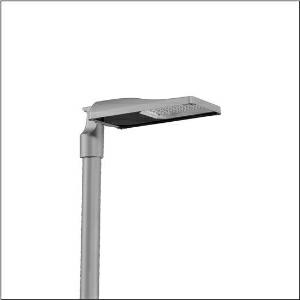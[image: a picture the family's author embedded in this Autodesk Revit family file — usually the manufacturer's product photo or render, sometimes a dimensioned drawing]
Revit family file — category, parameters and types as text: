
# Revit family: streetlight_sl_31_mini___st1_0a_5xh6d31b08ja_158d
name_source: partatom
category: Lighting Fixtures
units: mm (PartAtom-declared; Revit-internal decimal feet)

## family parameters
Cut with Voids When Loaded = No
Host = Face
Light Source = No
Part Type = Normal
Room Calculation Point = No
Round Connector Dimension = Use Diameter
Shared = No

## types (1)
- --- (1 x LED, 12140 lm, 81.1 W, 3000K)
    Apparent Load = 81 VA
    CIE Flux Codes = 40 73 97 100 100
    Color Rendering = 70
    Color Temperature = 3000K
    Default Elevation = 1800 mm
    Description = Streetlight SL 31 mini Easy, LST, Desk-Remote mast luminaire for post-top, side-entry; light control with lens of PMMA; light distribution: ST1.0a, direct asymmetric distribution, for standard-compliant lighting for roads and squares; LED: luminous flux: 12.140lm, light colour: 730, colour temperature: 3000K; luminous efficacy: 149,7lm/W; control: pre-setting: linear dimming characteristic, flexible luminous flux parameterisation, time-dependent luminous flux control, constant luminous flux control, power reduction, intelligent temperature release in ECG and LED module, overheat protection; luminaire housing, of diecast aluminium, SITECO metallic grey (DB 702S), corrosivity category C5 high according to DIN EN ISO 12944; cover of toughened safety glass, transparent, opened without tools; mast flange of diecast aluminium, SITECO metallic grey (DB 702S), spigot size: 76/60mm, mast flange included unmounted; with cable H07RN-F 5x 1.5mm², cable length: 10,5m, connection cable pre-assembled; mains connection: 220..240V, AC, 50/60Hz; power consumption (at start of service life): 81,1W / (at end of service life): 88,3W / (with reduced operation 50%): 36,4W; protection rating (complete): IP66; insulation class (complete): insulation class II (safety insulation); impact resistance: IK10; certification: CE, ENEC, ENEC+, VDE, UKCA; permissible operating ambient temperature for outdoor applications: -40..+50°C; packaging unit: 1 piece

Light Distribution: ST1.0a
    Height = 76 mm
    Lamp = 1 x LED
    Lamp Light Flux = 12140 lm
    Lamp Power = 81.1 W
    Lamp count = 1
    Length = 547 mm
    Luminous efficacy = 150 lm/W
    Manufacturer = Siteco
    ModVariant = No
    Model = 5XH6D31B08JA
    Number of Poles = 1
    OnlyDefault = Yes
    Power Factor = 1
    Product Name = Streetlight SL 31 mini | ST1.0a
    Product group = mast luminaire | pylon top
    ProductGroupID = 6100
    Protection Class = Protection class II
    Protection Degree = IP 66
    RLX_Detail_Level = 1
    RLX_Emergency_Light_Flux = 0 lm
    RLX_Emergency_Type = 0
    RLX_Emergency_Type_DB = No
    RlxData = <blob elided: 39677 chars, md5=14c8e815>
    Socket = socket
    Standby Power = 0 W
    System Light Flux = 12140 lm
    System Power = 81 W
    Type Comments = factory setting: luminous flux: 100 % | dim-lin: 254 | 860 mA
    Type Image = l_1300326.jpg
    URL = http://relux.com
    VarID = @adj_057315
    Voltage = 0 V
    Weight = 0.00 kg
    Width = 265 mm

## geometry (parser evidence)
native form markers: Blend x4, Sweep x9
no freeform markers — native parametric forms only
